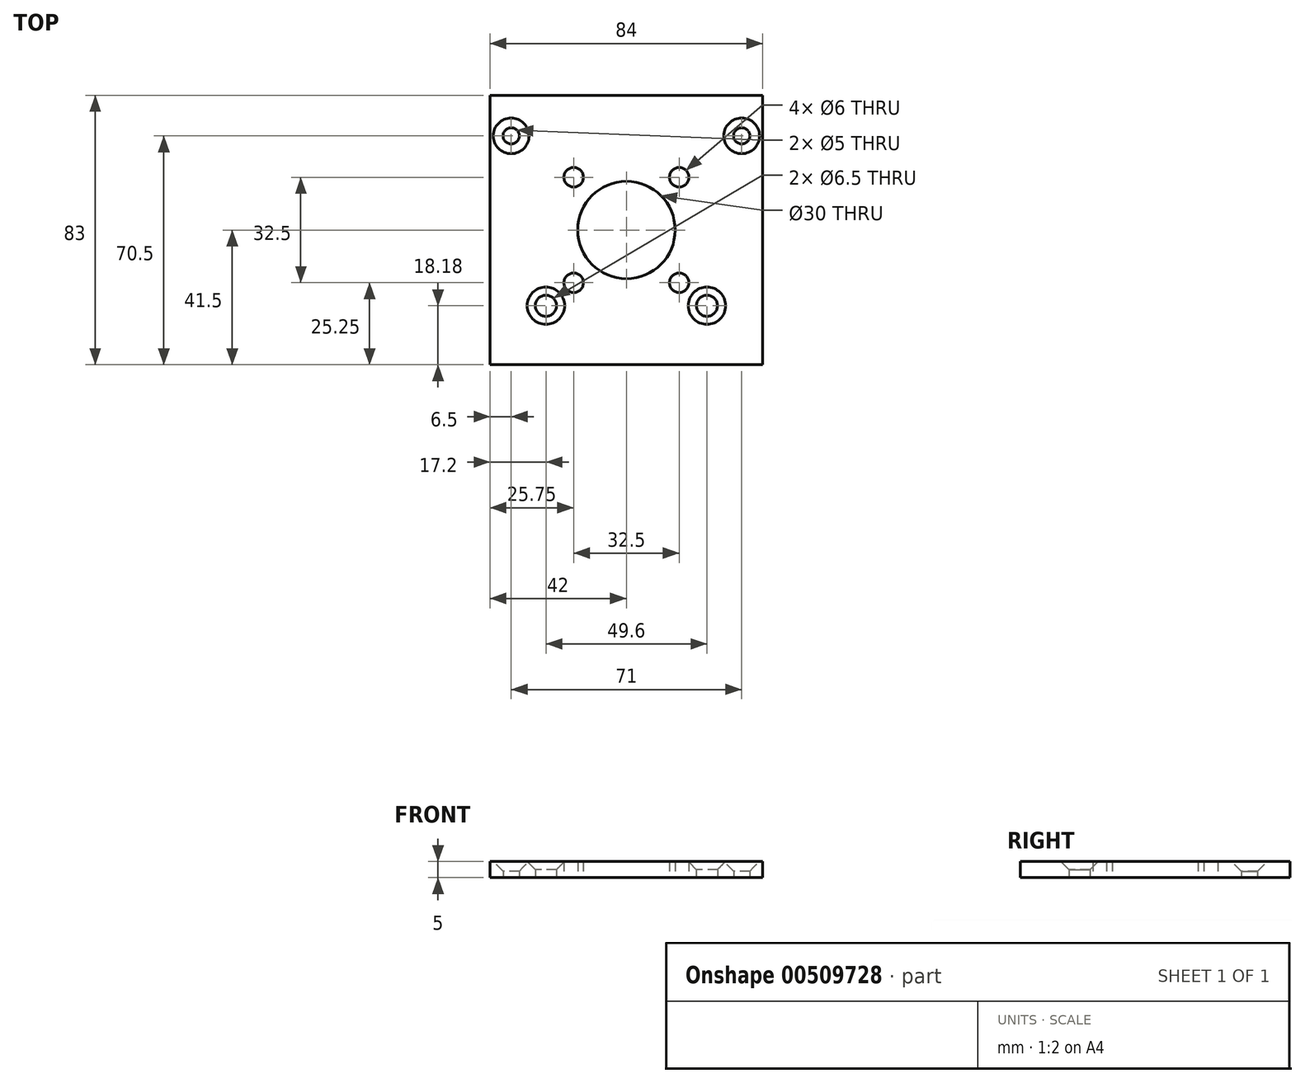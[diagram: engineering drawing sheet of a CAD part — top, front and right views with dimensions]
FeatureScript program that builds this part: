
annotation { "Feature Type Name" : "Feature", "Feature Type Description" : "" }
export const myFeature = defineFeature(function(context is Context, id is Id, definition is map)
    precondition{}
    {
        {
            var Q0;
            Q0=qCreatedBy(makeId("Top.planeOp"),FACE);
            var sketch = newSketch(context, id + "F0", { "sketchPlane" : qUnion([Q0])});
            skLineSegment(sketch, "E0.bottom", {"start": v(0, 0) * mm, "end": v(-84, 0) * mm});
            skLineSegment(sketch, "E0.top", {"start": v(0, 83) * mm, "end": v(-84, 83) * mm});
            skLineSegment(sketch, "E0.left", {"start": v(0, 0) * mm, "end": v(0, 83) * mm});
            skLineSegment(sketch, "E0.right", {"start": v(-84, 0) * mm, "end": v(-84, 83) * mm});
            skCircle(sketch, "E1", {"center": v(-77.5, 70.5) * mm, "radius": 2.5 * mm});
            skLineSegment(sketch, "E2", {"start": v(-84, 83) * mm, "end": v(-42, 83) * mm});
            skLineSegment(sketch, "E3", {"start": v(-42, 83) * mm, "end": v(-42, 0) * mm});
            skCircle(sketch, "E4.MirrorC", {"center": v(-6.5, 70.5) * mm, "radius": 2.5 * mm});
            skCircle(sketch, "E5", {"center": v(-66.8, 18.18) * mm, "radius": 3.25 * mm});
            skCircle(sketch, "E6.MirrorC", {"center": v(-17.2, 18.18) * mm, "radius": 3.25 * mm});
            skLineSegment(sketch, "E7", {"start": v(-84, 41.5) * mm, "end": v(0, 41.5) * mm});
            skCircle(sketch, "E8", {"center": v(-25.75, 25.25) * mm, "radius": 3 * mm});
            skCircle(sketch, "E9.MirrorC", {"center": v(-25.75, 57.75) * mm, "radius": 3 * mm});
            skLineSegment(sketch, "E10.MirrorCS", {"start": v(-42, 0) * mm, "end": v(-42, 83) * mm});
            skCircle(sketch, "E11.MirrorC", {"center": v(-58.25, 57.75) * mm, "radius": 3 * mm});
            skCircle(sketch, "E12.MirrorC", {"center": v(-58.25, 25.25) * mm, "radius": 3 * mm});
            skCircle(sketch, "E13", {"center": v(-42, 41.5) * mm, "radius": 15 * mm});
            skSolve(sketch);
        }
        {
            var Q0;
            Q0 = qSketchRegion(id + "F0", true);
            extrude(context, id + "F1", {"entities" : qUnion([Q0]), "depth" : 5 * mm});
        }
        {
            var Q0;
            Q0=makeQuery(id+"F1.opExtrude","CAP_EDGE",EDGE,{"disambiguationData":[OSD([sQuery(id+"F0.wireOp",EDGE,"E1")])],"isStart":false});
            chamfer(context, id + "F2", {"entities" : qUnion([Q0]), "width" : 3 * mm, "tangentPropagation" : true});
        }
        {
            var Q0;
            Q0=makeQuery(id+"F1.opExtrude","CAP_EDGE",EDGE,{"disambiguationData":[OSD([sQuery(id+"F0.wireOp",EDGE,"E4.MirrorC")])],"isStart":false});
            chamfer(context, id + "F3", {"entities" : qUnion([Q0]), "width" : 3 * mm, "tangentPropagation" : true});
        }
        {
            var Q0;
            Q0=makeQuery(id+"F1.opExtrude","CAP_EDGE",EDGE,{"disambiguationData":[OSD([sQuery(id+"F0.wireOp",EDGE,"E5")])],"isStart":false});
            chamfer(context, id + "F4", {"entities" : qUnion([Q0]), "width" : 2.5 * mm, "tangentPropagation" : true});
        }
        {
            var Q0;
            Q0=makeQuery(id+"F1.opExtrude","CAP_EDGE",EDGE,{"disambiguationData":[OSD([sQuery(id+"F0.wireOp",EDGE,"E6.MirrorC")])],"isStart":false});
            chamfer(context, id + "F5", {"entities" : qUnion([Q0]), "width" : 2.5 * mm, "tangentPropagation" : true});
        }
    });
